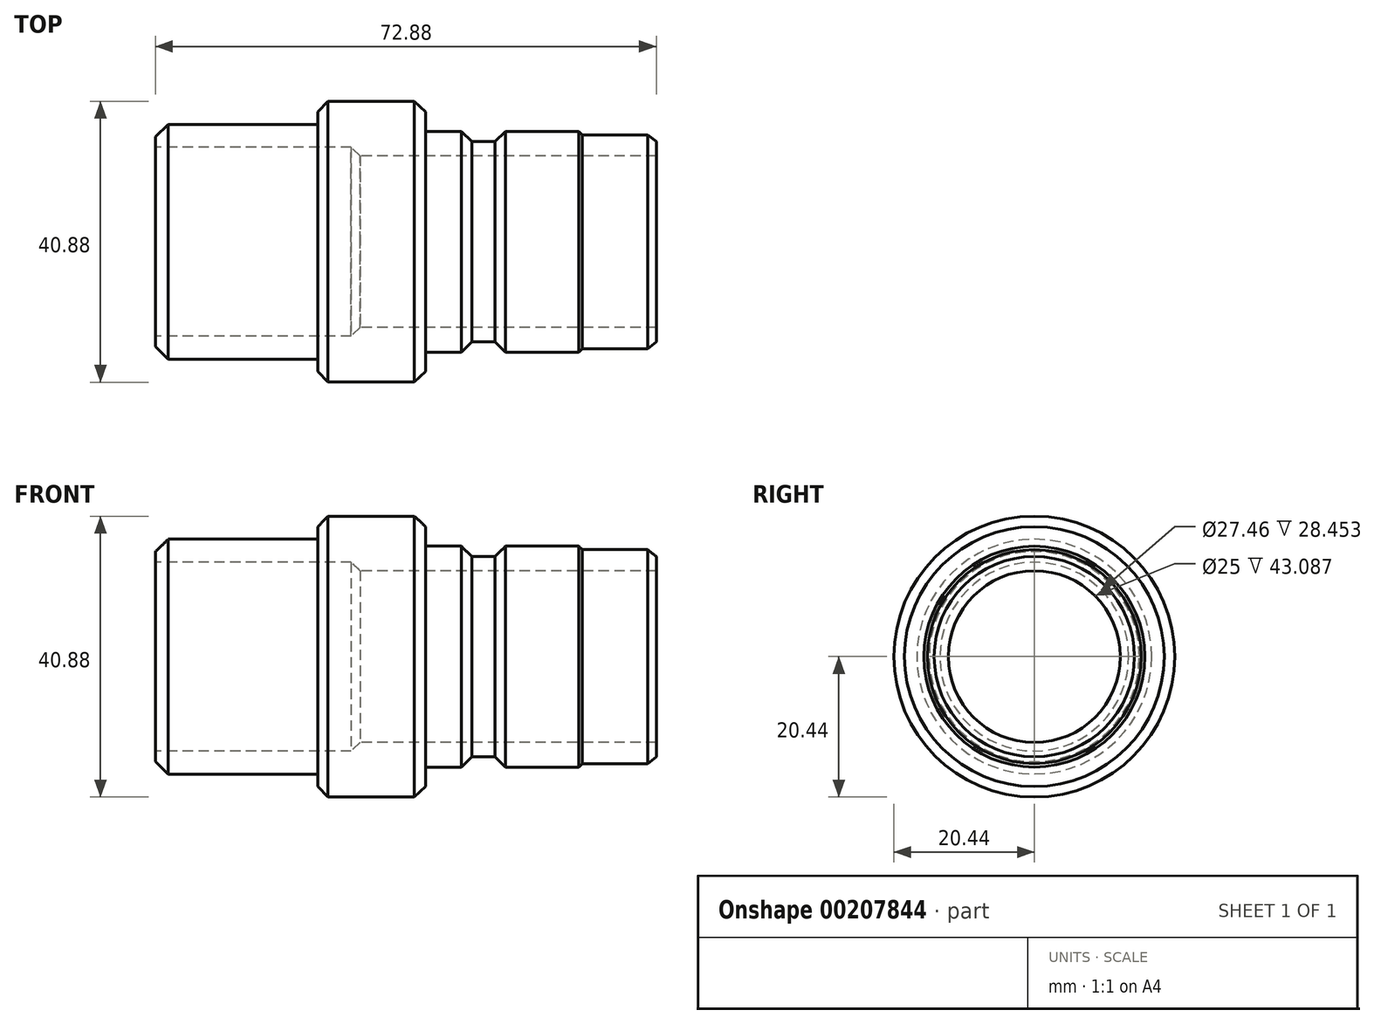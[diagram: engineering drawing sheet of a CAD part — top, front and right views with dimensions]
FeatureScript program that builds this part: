
annotation { "Feature Type Name" : "Feature", "Feature Type Description" : "" }
export const myFeature = defineFeature(function(context is Context, id is Id, definition is map)
    precondition{}
    {
        {
            var Q0;
            Q0=qCreatedBy(makeId("Front.planeOp"),FACE);
            var sketch = newSketch(context, id + "F0", { "sketchPlane" : qUnion([Q0])});
            skLineSegment(sketch, "E0", {"start": v(0, 0) * mm, "end": v(73, 0) * mm});
            skLineSegment(sketch, "E1", {"start": v(72.88, 12.5) * mm, "end": v(29.8, 12.5) * mm});
            skLineSegment(sketch, "E2", {"start": v(29.8, 12.5) * mm, "end": v(28.45, 13.73) * mm});
            skLineSegment(sketch, "E3", {"start": v(28.45, 13.73) * mm, "end": v(0, 13.73) * mm});
            skLineSegment(sketch, "E4", {"start": v(23.64, 17.08) * mm, "end": v(23.64, 18.9) * mm});
            skLineSegment(sketch, "E5", {"start": v(23.64, 18.9) * mm, "end": v(25.1, 20.44) * mm});
            skLineSegment(sketch, "E6", {"start": v(25.1, 20.44) * mm, "end": v(37.68, 20.44) * mm});
            skLineSegment(sketch, "E7", {"start": v(37.68, 20.44) * mm, "end": v(39.33, 18.9) * mm});
            skLineSegment(sketch, "E8", {"start": v(39.33, 18.9) * mm, "end": v(39.33, 16.07) * mm});
            skLineSegment(sketch, "E9", {"start": v(39.33, 16.07) * mm, "end": v(44.53, 16.07) * mm});
            skLineSegment(sketch, "E10", {"start": v(44.53, 16.07) * mm, "end": v(46.02, 14.57) * mm});
            skLineSegment(sketch, "E11", {"start": v(46.02, 14.57) * mm, "end": v(49.38, 14.57) * mm});
            skLineSegment(sketch, "E12", {"start": v(49.38, 14.57) * mm, "end": v(50.92, 16.07) * mm});
            skLineSegment(sketch, "E13", {"start": v(50.92, 16.07) * mm, "end": v(61.6, 16.07) * mm});
            skLineSegment(sketch, "E14", {"start": v(61.6, 16.07) * mm, "end": v(62.12, 15.56) * mm});
            skLineSegment(sketch, "E15", {"start": v(62.12, 15.56) * mm, "end": v(71.63, 15.56) * mm});
            skLineSegment(sketch, "E16", {"start": v(71.63, 15.56) * mm, "end": v(72.88, 14.57) * mm});
            skLineSegment(sketch, "E17", {"start": v(72.88, 14.57) * mm, "end": v(72.88, 12.5) * mm});
            skLineSegment(sketch, "E18", {"start": v(23.64, 17.08) * mm, "end": v(1.85, 17.08) * mm});
            skLineSegment(sketch, "E19", {"start": v(1.85, 17.08) * mm, "end": v(0, 15.29) * mm});
            skLineSegment(sketch, "E20", {"start": v(0, 15.29) * mm, "end": v(0, 13.73) * mm});
            skSolve(sketch);
        }
        {
            var Q0;
            Q0 = qSketchRegion(id + "F0", true);
            var Q1;
            Q1=sQuery(id+"F0.wireOp",EDGE,"E0");
            revolve(context, id + "F1", {"entities" : qUnion([Q0]), "axis" : qUnion([Q1]), "revolveType" : RevolveType.FULL});
        }
    });
